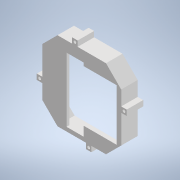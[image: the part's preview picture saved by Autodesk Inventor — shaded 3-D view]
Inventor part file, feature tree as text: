
AUTODESK INVENTOR PART (.ipt)
format: ipt  version: 2021.2 (Build 252289000, 289)  size: 206,848 bytes
history: native  units: mm
features: reference x17, other x5, extrude x4, sketch x4, projected_geometry x1
ambient origin geometry x8: Origin, YZ Plane, XZ Plane, XY Plane, X Axis, Y Axis, Z Axis, Center Point
bodies: Body1 (feature_tree)
feature tree (31):
  other  "Твердое тело1"
  extrude  "Выдавливание1"  Depth=1.5mm
  extrude  "Выдавливание2"  Depth=1.0mm
  extrude  "Выдавливание3"  Depth=0.5mm
  extrude  "Выдавливание4"  Depth=2.0mm TaperAngle=0.0deg
  sketch  "Эскиз1"
  reference  "Ссылка1"
  reference  "Ссылка2"
  reference  "Ссылка3"
  reference  "Ссылка4"
  reference  "Ссылка5"
  reference  "Ссылка6"
  reference  "Ссылка7"
  reference  "Ссылка8"
  reference  "Ссылка9"
  reference  "Ссылка10"
  reference  "Ссылка11"
  reference  "Ссылка12"
  reference  "Ссылка13"
  sketch  "Эскиз2"
  projected_geometry  "Спроецированная петля1"
  sketch  "Эскиз3"
  sketch  "Эскиз4"
  reference  "Ссылка14"
  reference  "Ссылка15"
  reference  "Ссылка16"
  reference  "Ссылка17"
  parser-record x1  (decoder bookkeeping rows leaked as tree rows — omitted from the tree; the rows remain in map.json)
  other  "Сборка1.iam"
  other  "Плата печатная2:1"
  other  "Середина:1"
note: 1 file-system path scrubbed to <path> (originals preserved in map.json)
